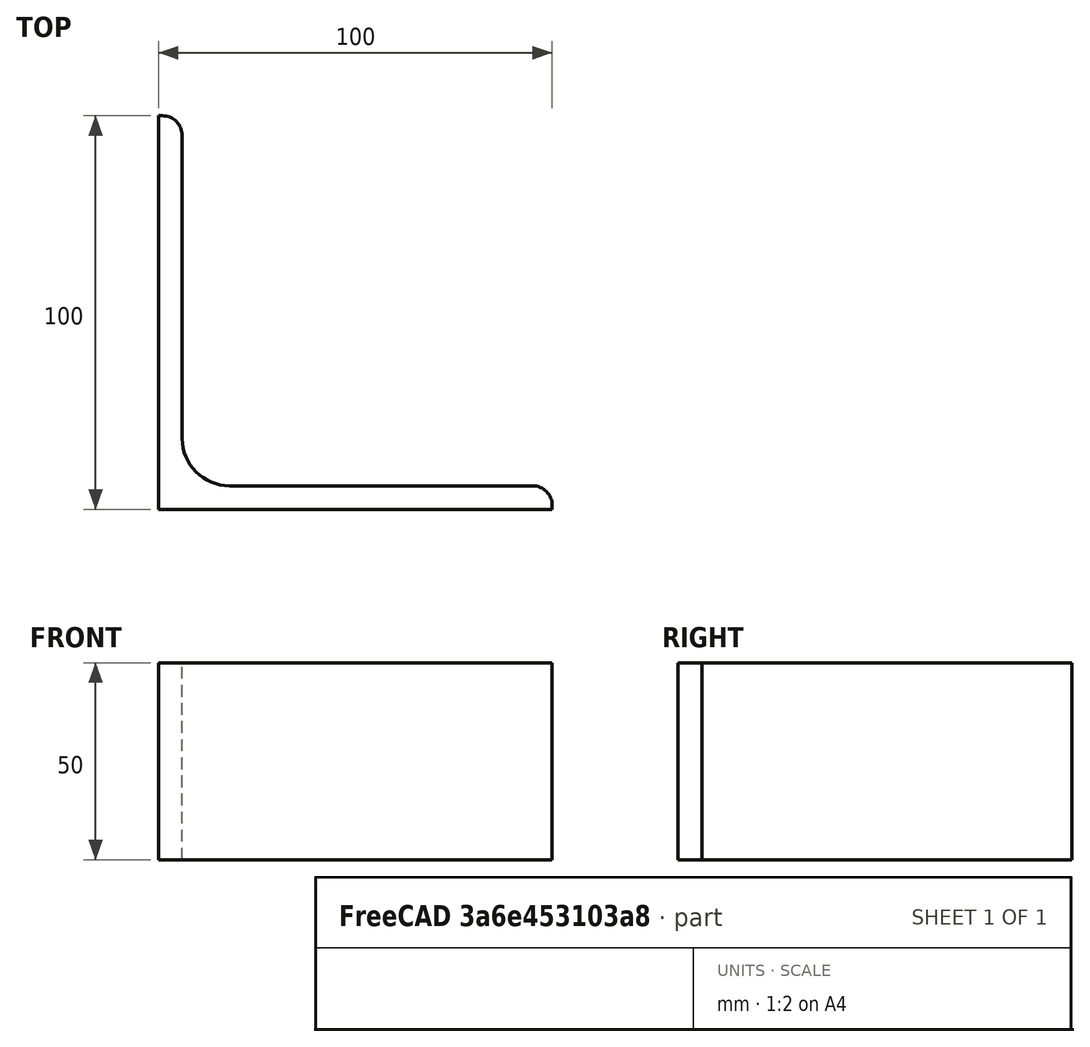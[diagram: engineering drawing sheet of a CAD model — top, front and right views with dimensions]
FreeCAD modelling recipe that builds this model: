
FCSTD DOCUMENT  (FreeCAD 0.15R4671 (Git))
Label: Angle Bar L100x100x6 EN10056 S235JR
License: All rights reserved
LicenseURL: http://en.wikipedia.org/wiki/All_rights_reserved
objects: Sketcher::SketchObject×1, Part::Extrusion×1
note: 2 computed .brp shape members not serialized (recipe doc carries the construction recipe); baked Part::Feature solids carry a one-line shape summary decoded from their .brp

FEATURE [Sketcher::SketchObject] Sketch
  sketch-geometry (9):
    g0: LineSegment StartX=0 StartY=0 StartZ=0 EndX=100 EndY=0 EndZ=0
    g1: LineSegment StartX=100 StartY=0 StartZ=0 EndX=100 EndY=1 EndZ=0
    g2: LineSegment StartX=95 StartY=6 StartZ=0 EndX=18 EndY=6 EndZ=0
    g3: LineSegment StartX=0 StartY=0 StartZ=0 EndX=0 EndY=100 EndZ=0
    g4: LineSegment StartX=0 StartY=100 StartZ=0 EndX=1 EndY=100 EndZ=0
    g5: LineSegment StartX=6 StartY=95 StartZ=0 EndX=6 EndY=18 EndZ=0
    g6: ArcOfCircle CenterX=18 CenterY=18 CenterZ=0 NormalX=0 NormalY=0 NormalZ=1 Radius=12 StartAngle=3.14159 EndAngle=4.71239
    g7: ArcOfCircle CenterX=1 CenterY=95 CenterZ=0 NormalX=0 NormalY=0 NormalZ=1 Radius=5 StartAngle=0 EndAngle=1.5708
    g8: ArcOfCircle CenterX=95 CenterY=1 CenterZ=0 NormalX=0 NormalY=0 NormalZ=1 Radius=5 StartAngle=0 EndAngle=1.5708
  constraints (23):
    c: Coincident(g0,g-1)
    c: Horizontal(g0)
    c: Coincident(g1,g0)
    c: Vertical(g1)
    c: Horizontal(g2)
    c: Coincident(g3,g-1)
    c: Vertical(g3)
    c: Coincident(g4,g3)
    c: Horizontal(g4)
    c: Vertical(g5)
    c: Tangent(g5,g6) = -1.5708
    c: Tangent(g2,g6) = 1.5708
    c: Tangent(g4,g7) = 1.5708
    c: Tangent(g5,g7) = 1.5708
    c: Tangent(g2,g8) = -1.5708
    c: Tangent(g1,g8) = -1.5708
    c: DistanceX(g0) = 100
    c: DistanceY(g3) = 100
    c: DistanceY(g0,g2) = 6
    c: DistanceX(g3,g5) = 6
    c: Radius(g6) = 12
    c: Radius(g8) = 5
    c: Radius(g7) = 5
FEATURE [Part::Extrusion] Extrude  label="Angle Bar L100x100x6 EN10056 S235JR"
  Base = -> Sketch
  Dir = (0,0,50)
  Solid = true
